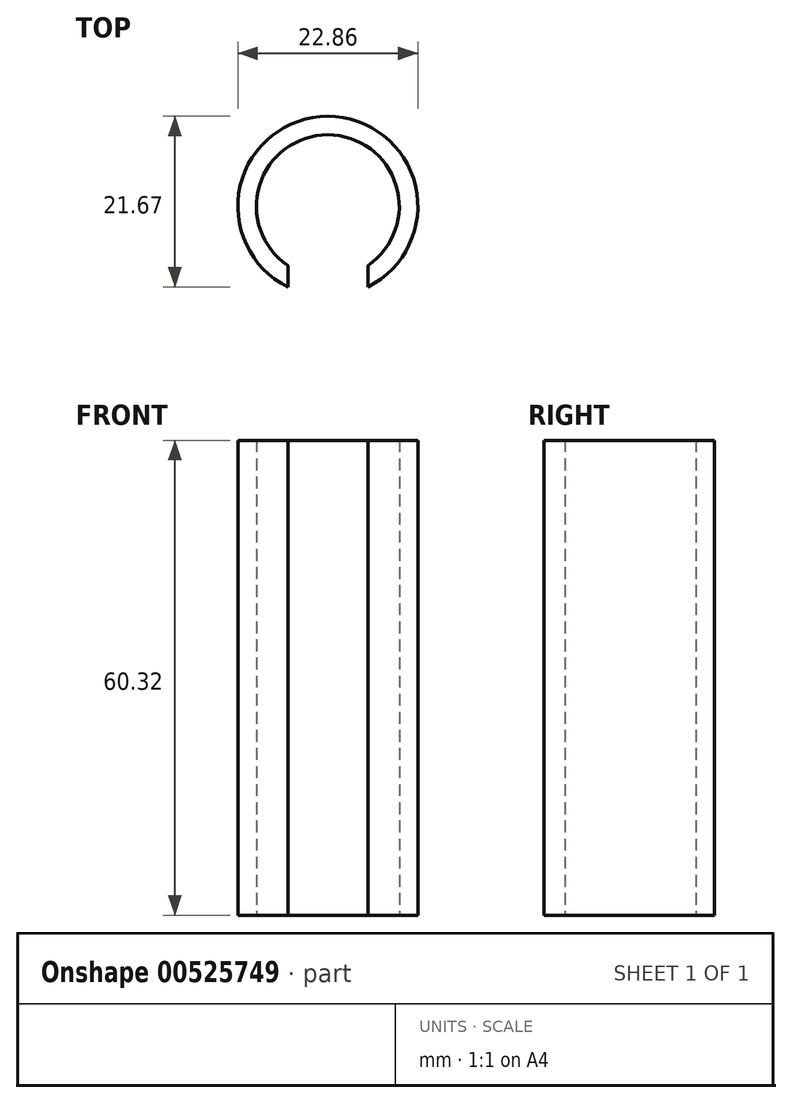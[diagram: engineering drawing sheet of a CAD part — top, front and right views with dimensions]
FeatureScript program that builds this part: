
annotation { "Feature Type Name" : "Feature", "Feature Type Description" : "" }
export const myFeature = defineFeature(function(context is Context, id is Id, definition is map)
    precondition{}
    {
        {
            var Q0;
            Q0=qCreatedBy(makeId("Top.planeOp"),FACE);
            var sketch = newSketch(context, id + "F0", { "sketchPlane" : qUnion([Q0])});
            skCircle(sketch, "E0", {"center": v(0, 0) * mm, "radius": 9.08 * mm});
            skCircle(sketch, "E1", {"center": v(0, 0) * mm, "radius": 11.43 * mm});
            skSolve(sketch);
        }
        {
            var Q0;
            Q0=makeQuery(id+"F0.imprint","IMPRINT",FACE,{"disambiguationData":[TD([[makeQuery(id+"F0.imprint","IMPRINT",EDGE,{"derivedFrom":sQuery(id+"F0.wireOp",EDGE,"E0")}),-1.0]])]});
            extrude(context, id + "F1", {"entities" : qUnion([Q0]), "depth" : 60.32 * mm, "offsetDistance" : 25.4 * mm});
        }
        {
            var Q0;
            Q0=qCreatedBy(makeId("Top.planeOp"),FACE);
            var sketch = newSketch(context, id + "F2", { "sketchPlane" : qUnion([Q0])});
            skLineSegment(sketch, "E2", {"start": v(0, 0) * mm, "end": v(5.08, 0) * mm});
            skLineSegment(sketch, "E3", {"start": v(5.08, 0) * mm, "end": v(5.08, -15.77) * mm});
            skLineSegment(sketch, "E4", {"start": v(5.08, -15.77) * mm, "end": v(-5.08, -15.77) * mm});
            skLineSegment(sketch, "E5", {"start": v(-5.08, -15.77) * mm, "end": v(-5.08, 0) * mm});
            skLineSegment(sketch, "E6", {"start": v(-5.08, 0) * mm, "end": v(0, 0) * mm});
            skSolve(sketch);
        }
        {
            var Q0;
            Q0=makeQuery(id+"F2.imprint","IMPRINT",FACE,{"disambiguationData":[TD([[makeQuery(id+"F2.imprint","IMPRINT",EDGE,{"derivedFrom":sQuery(id+"F2.wireOp",EDGE,"E2")}),-1.0]])]});
            extrude(context, id + "F3", {"entities" : qUnion([Q0]), "operationType" : NewBodyOperationType.REMOVE, "depth" : 127 * mm, "offsetDistance" : 25.4 * mm});
        }
    });
